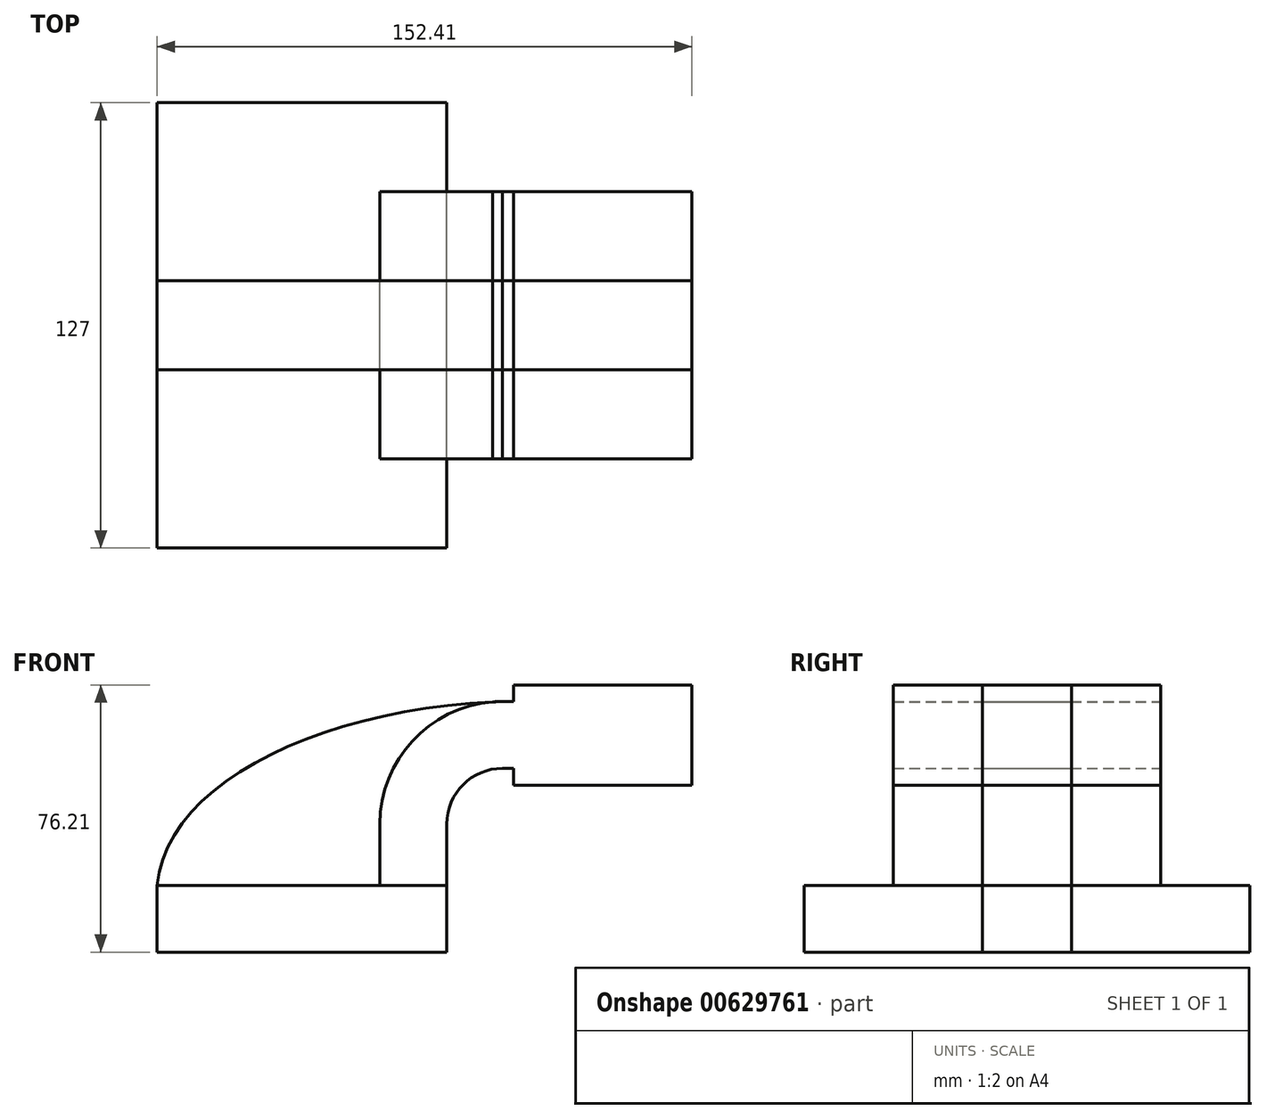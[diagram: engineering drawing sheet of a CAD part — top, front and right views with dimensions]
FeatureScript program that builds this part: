
annotation { "Feature Type Name" : "Feature", "Feature Type Description" : "" }
export const myFeature = defineFeature(function(context is Context, id is Id, definition is map)
    precondition{}
    {
        {
            var Q0;
            Q0=qCreatedBy(makeId("Front.planeOp"),FACE);
            var sketch = newSketch(context, id + "F0", { "sketchPlane" : qUnion([Q0])});
            skLineSegment(sketch, "E0.bottom", {"start": v(41.28, -9.52) * mm, "end": v(-41.28, -9.53) * mm});
            skLineSegment(sketch, "E0.top", {"start": v(41.28, 9.53) * mm, "end": v(-41.28, 9.52) * mm});
            skLineSegment(sketch, "E0.left", {"start": v(41.28, -9.52) * mm, "end": v(41.28, 9.53) * mm});
            skLineSegment(sketch, "E0.right", {"start": v(-41.28, -9.53) * mm, "end": v(-41.28, 9.52) * mm});
            skPoint(sketch, "E0.middle", {"position": v(0, 0) * mm});
            skLineSegment(sketch, "E1", {"start": v(41.28, 9.53) * mm, "end": v(41.28, 27) * mm});
            skArc(sketch, "E2", {"start": v(41.28, 27) * mm, "mid": v(45.92, 38.23) * mm, "end": v(57.15, 42.88) * mm});
            skLineSegment(sketch, "E3.bottom", {"start": v(111.12, 38.1) * mm, "end": v(60.33, 38.1) * mm});
            skLineSegment(sketch, "E3.top", {"start": v(111.12, 66.68) * mm, "end": v(60.33, 66.68) * mm});
            skLineSegment(sketch, "E3.left", {"start": v(111.12, 38.1) * mm, "end": v(111.12, 66.68) * mm});
            skLineSegment(sketch, "E3.right", {"start": v(60.33, 38.1) * mm, "end": v(60.33, 66.68) * mm});
            skPoint(sketch, "E3.middle", {"position": v(85.72, 52.39) * mm});
            skLineSegment(sketch, "E4", {"start": v(57.15, 42.88) * mm, "end": v(85.54, 42.88) * mm});
            skLineSegment(sketch, "E5.0", {"start": v(57.15, 61.93) * mm, "end": v(85.57, 61.93) * mm});
            skArc(sketch, "E5.1", {"start": v(22.23, 27) * mm, "mid": v(32.45, 51.7) * mm, "end": v(57.15, 61.93) * mm});
            skLineSegment(sketch, "E5.2", {"start": v(22.23, 9.53) * mm, "end": v(22.23, 27) * mm});
            skLineSegment(sketch, "E6", {"start": v(85.72, 38.1) * mm, "end": v(85.54, 66.68) * mm});
            skFitSpline(sketch, "E7", {"points": [v(-41.28, 9.52) * mm, v(57.15, 61.93) * mm], "startDerivative": vector(7.82, 88.57) * mm, "endDerivative": vector(152.45, 5.1) * mm});
            skSolve(sketch);
        }
        {
            var Q0;
            {var subQ9=sQuery(id+"F0.wireOp",EDGE,"E1");Q0=makeQuery(id+"F0.imprint","IMPRINT",FACE,{"disambiguationData":[TD([[makeQuery(id+"F0.imprint","IMPRINT",EDGE,{"derivedFrom":subQ9}),1.0]])]});}
            var Q1;
            {var subQ4=sQuery(id+"F0.wireOp",EDGE,"E3.left");Q1=makeQuery(id+"F0.imprint","IMPRINT",FACE,{"disambiguationData":[TD([[makeQuery(id+"F0.imprint","IMPRINT",EDGE,{"derivedFrom":subQ4}),1.0]])]});}
            var Q2;
            {var subQ0=sQuery(id+"F0.wireOp",EDGE,"E3.right");var subQ1=sQuery(id+"F0.wireOp",EDGE,"E3.top");var subQ2=makeQuery(id+"F0.imprint","INTERSECT",VERTEX,{"derivedFrom":[subQ1,subQ0]});Q2=makeQuery(id+"F0.imprint","IMPRINT",FACE,{"disambiguationData":[TD([[makeQuery(id+"F0.imprint","IMPRINT",EDGE,{"disambiguationData":[TD([[subQ2,1.0]])],"derivedFrom":subQ1}),1.0]])]});}
            var Q3;
            {var subQ3=sQuery(id+"F0.wireOp",EDGE,"E3.right");var subQ5=sQuery(id+"F0.wireOp",EDGE,"E3.bottom");var subQ6=makeQuery(id+"F0.imprint","INTERSECT",VERTEX,{"derivedFrom":[subQ5,subQ3]});Q3=makeQuery(id+"F0.imprint","IMPRINT",FACE,{"disambiguationData":[TD([[makeQuery(id+"F0.imprint","IMPRINT",EDGE,{"disambiguationData":[TD([[subQ6,1.0]])],"derivedFrom":subQ5}),-1.0]])]});}
            extrude(context, id + "F1", {"entities" : qUnion([Q0, Q1, Q2, Q3]), "endBound" : BoundingType.SYMMETRIC, "depth" : 76.2 * mm, "offsetDistance" : 25.4 * mm});
        }
        {
            var Q0;
            Q0=makeQuery(id+"F0.imprint","IMPRINT",FACE,{"disambiguationData":[TD([[makeQuery(id+"F0.imprint","IMPRINT",EDGE,{"derivedFrom":sQuery(id+"F0.wireOp",EDGE,"E0.bottom")}),-1.0]])]});
            extrude(context, id + "F2", {"entities" : qUnion([Q0]), "endBound" : BoundingType.SYMMETRIC, "depth" : 127 * mm, "offsetDistance" : 25.4 * mm});
        }
        {
            var Q0;
            Q0 = qSketchRegion(id + "F0", true);
            extrude(context, id + "F3", {"entities" : qUnion([Q0]), "endBound" : BoundingType.SYMMETRIC, "depth" : 25.4 * mm, "offsetDistance" : 25.4 * mm});
        }
    });
